# Revit family: VALVULADA PESADA
name_source: partatom
category: Pipe Accessories
units: mm (PartAtom-declared; Revit-internal decimal feet)

## family parameters
Always vertical = Yes
Cut with Voids When Loaded = No
Part Type = Valve - Breaks Into
Round Connector Dimension = Use Diameter
Shared = No
Work Plane-Based = No

## types (6) — shared parameters
Description = VÁLVULAS DE BOLA COMPACTAS EN PVC PARA APLICACIONES TIPO PESADO
Imagen = https://pcpplasticos.co
Manufacturer = PCP PLASTICOS
URL = https://pcpplasticos.co
zero-valued in all types: Default Elevation

## per-type parameters (varying)
| type | 1 1/2" | 1 1/4" | 1" | 1/2" | 2" | 3/4" | Diametro | Dist. 1 | Dist. 2 | Model | SKU |
| Diametro 1/2" | No | No | No | Yes | No | No | 12.7 mm  [stored 0.0416667 ft] | 40 mm  [stored 0.131234 ft] | 39.2 mm  [stored 0.128609 ft] | 3011 | 3011 |
| Diametro 1" | No | No | Yes | No | No | No | 25.4 mm  [stored 0.0833333 ft] | 49.9 mm  [stored 0.163714 ft] | 49.1 mm  [stored 0.161089 ft] | 3041 | 3041 |
| Diametro 1 1/4" | No | Yes | No | No | No | No | 31.75 mm | 53 mm  [stored 0.173885 ft] | 52.2 mm  [stored 0.17126 ft] | 3084 | 3084 |
| Diametro 3/4" | No | No | No | No | No | Yes | 19.05 mm  [stored 0.0625 ft] | 45.8 mm | 45 mm  [stored 0.147638 ft] | 3039 | 3039 |
| Diametro 1 1/2" | Yes | No | No | No | No | No | 38.1 mm  [stored 0.125 ft] | 59.5 mm  [stored 0.19521 ft] | 58.7 mm  [stored 0.192585 ft] | 3070 | 3070 |
| Diametro 2" | No | No | No | No | Yes | No | 50.8 mm  [stored 0.166667 ft] | 65.8 mm  [stored 0.215879 ft] | 65 mm  [stored 0.213255 ft] | 3074 | 3074 |

note: [stored X ft] marks values corroborated as IEEE doubles in the binary element streams (Revit-internal decimal feet)

## geometry (parser evidence)
native form markers: Sweep x2
no freeform markers — native parametric forms only
